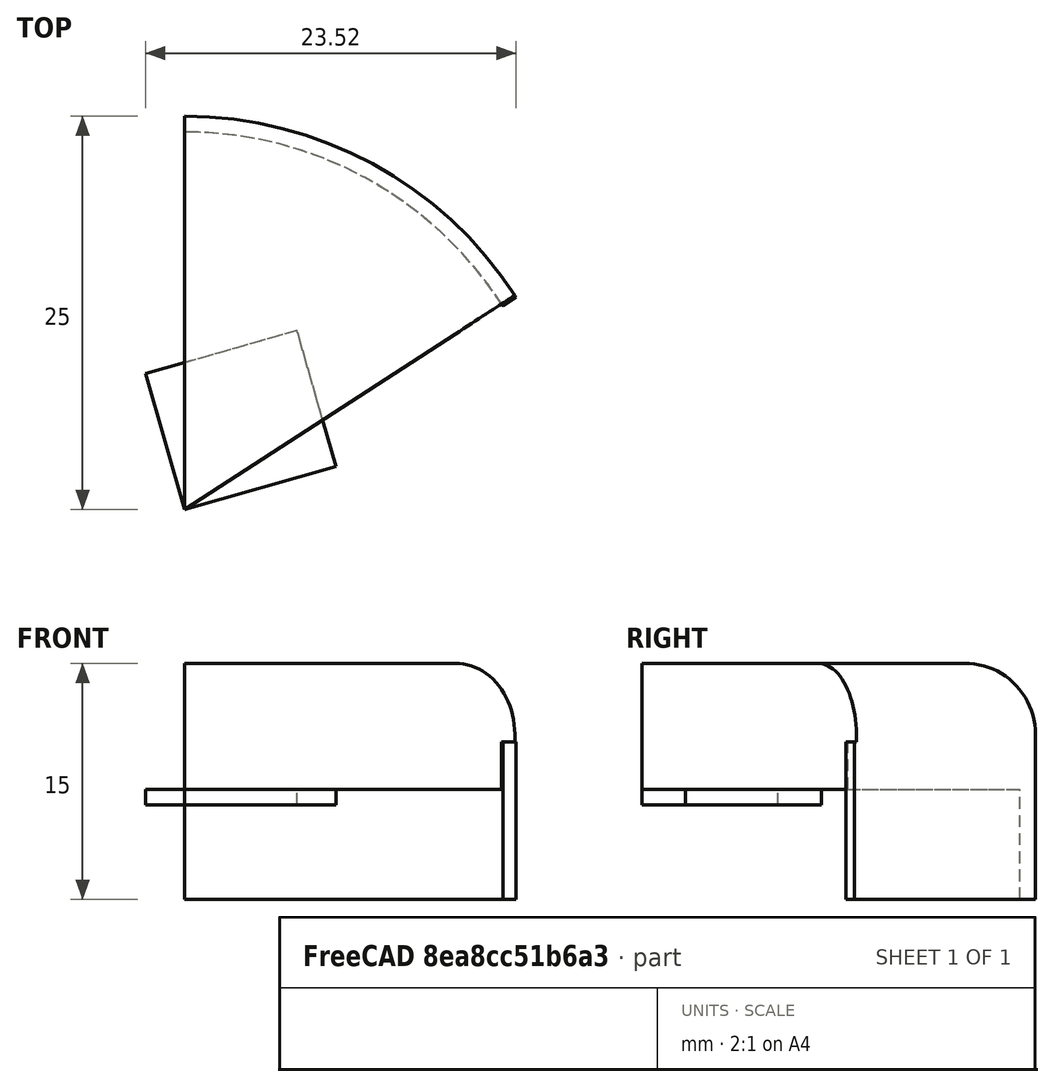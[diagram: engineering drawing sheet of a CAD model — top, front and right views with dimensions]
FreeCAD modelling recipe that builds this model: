
FCSTD DOCUMENT  (FreeCAD 0.14R3700 (Git))
Label: tapa de la tapa
License: CC-BY 3.0
LicenseURL: http://creativecommons.org/licenses/by/3.0/
objects: Part::Cylinder×7, Part::Cut×5, Part::Box×5, Part::MultiFuse×3, Part::Fillet×1, Part::MultiCommon×1
note: 22 computed .brp shape members not serialized (recipe doc carries the construction recipe); baked Part::Feature solids carry a one-line shape summary decoded from their .brp

FEATURE [Part::Cylinder] Cylinder  label="Cilindro"
  Angle = 360
  Height = 40
  Radius = 25
FEATURE [Part::Cylinder] Cylinder001  label="Cilindro001"
  Angle = 360
  Height = 37
  Radius = 22
FEATURE [Part::Cylinder] Cylinder002  label="Cilindro002"
  Angle = 360
  Height = 5
  Placement = pos=(0,0,40) rot=(0,0,1;0rad)
  Radius = 25
FEATURE [Part::Cylinder] Cylinder003  label="Cilindro003"
  Angle = 360
  Height = 10
  Radius = 23
FEATURE [Part::Cylinder] Cylinder004  label="Cilindro004"
  Angle = 360
  Height = 21
  Radius = 21
FEATURE [Part::Fillet] Fillet
  Base = -> Cylinder002
  Edges = 1 edges r=4.5: [Edge1]
FEATURE [Part::Cut] Cut
  Base = -> Cylinder
  Tool = -> Cylinder001
FEATURE [Part::Cut] Cut001
  Base = -> Cylinder003
  Placement = pos=(0,0,-5) rot=(0,0,1;0rad)
  Tool = -> Cylinder004
FEATURE [Part::Box] Box  label="Cubo"
  Height = 10
  Length = 37
  Placement = pos=(0,0,37) rot=(0,0,1;0rad)
  Width = 39
FEATURE [Part::Box] Box001  label="Cubo001"
  Height = 10
  Length = 37
  Placement = pos=(0,0,37) rot=(0,0,-1;0.994838rad)
  Width = 39
FEATURE [Part::Cut] Cut002
  Base = -> Box
  Tool = -> Box001
FEATURE [Part::MultiFuse] Fusion
  Shapes = -> [Fillet,Cut,Cut001]
FEATURE [Part::MultiCommon] Common
  Shapes = -> [Cut002,Fusion]
FEATURE [Part::Box] Box002  label="Cubo002"
  Height = 1
  Length = 10
  Placement = pos=(0,0,36) rot=(0,0,1;0.279253rad)
  Width = 9
FEATURE [Part::Cylinder] Cylinder005  label="Cilindro005"
  Angle = 360
  Height = 10
  Placement = pos=(0,0,34) rot=(0,0,1;0rad)
  Radius = 25
FEATURE [Part::Cylinder] Cylinder006  label="Cilindro006"
  Angle = 360
  Height = 10
  Placement = pos=(0,0,34) rot=(0,0,1;0rad)
  Radius = 24
FEATURE [Part::Box] Box003  label="Cubo003"
  Height = 17
  Length = 33
  Placement = pos=(-29,-19,29) rot=(0,0,-1;0.994838rad)
  Width = 70
FEATURE [Part::Box] Box004  label="Cubo004"
  Height = 17
  Length = 33
  Placement = pos=(-33,-19,29) rot=(0,0,1;0rad)
  Width = 70
FEATURE [Part::MultiFuse] Fusion001
  Shapes = -> [Box003,Box004]
FEATURE [Part::Cut] Cut003
  Base = -> Cylinder005
  Tool = -> Cylinder006
FEATURE [Part::Cut] Cut004
  Base = -> Cut003
  Placement = pos=(0,0,-4) rot=(0,0,1;0rad)
  Tool = -> Fusion001
FEATURE [Part::MultiFuse] Fusion002
  Shapes = -> [Cut004,Box002,Common]
